# Revit family: Burko F-2750
name_source: partatom
category: HLS-Bauteile
units: mm (PartAtom-declared; Revit-internal decimal feet)

## family parameters
Arbeitsebenenbasiert = Nein
Beim Laden mit Abzugskörper schneiden = Nein
Bemaßung runder Anschluss = Durchmesser verwenden
Beschriftungsausrichtung beibehalten = Nein
Gemeinsam genutzt = Nein
Immer vertikal = Ja
Klassifizierung = Keine
Raumberechnungspunkt = Nein
Teiletyp = Normal

## types (4) — shared parameters
Anschluss_1" = 25 mm  [stored 0.082021 ft]
Anschluss_3/4" = 20 mm  [stored 0.0656168 ft]
Datenblatt = https://www.burkhalter-h2o.ch
Homepage = https://www.burkhalter-h2o.ch
LUT = LUT_Burko_F-2750
Steuerung_Tiefe = 75 mm  [stored 0.246063 ft]
zero-valued in all types: Vorgabe-Ansicht

## per-type parameters (varying)
| type | A | B | Behälterkopf | C | Harzinhalt_pro_Harzdruckbehälter | Hauptsäule_Durchmesser | Sockel_Absatz_Oben | Sockel_Absatz_Unten | Sockel_Höhe | Steuerung_Breite | Steuerung_Höhe |
| Burko F-2750 - 25L | 257 mm  [stored 0.843176 ft] | 1110 mm  [stored 3.64173 ft] | 100 mm  [stored 0.328084 ft] | 1050 mm  [stored 3.44488 ft] | 25L | 75 mm  [stored 0.246063 ft] | 139 mm | 139 mm | 100 mm  [stored 0.328084 ft] | 175 mm  [stored 0.574147 ft] | 150 mm  [stored 0.492126 ft] |
| Burko F-2750 - 50L | 304 mm  [stored 0.997375 ft] | 1440 mm  [stored 4.72441 ft] | 150 mm  [stored 0.492126 ft] | 1380 mm  [stored 4.52756 ft] | 50L | 100 mm  [stored 0.328084 ft] | 162 mm  [stored 0.531496 ft] | 162 mm  [stored 0.531496 ft] | 100 mm  [stored 0.328084 ft] | 175 mm  [stored 0.574147 ft] | 150 mm  [stored 0.492126 ft] |
| Burko F-2750 - 75L | 369 mm  [stored 1.21063 ft] | 1880 mm  [stored 6.16798 ft] | 150 mm  [stored 0.492126 ft] | 1820 mm  [stored 5.97113 ft] | 75L | 100 mm  [stored 0.328084 ft] | 195 mm  [stored 0.639764 ft] | 195 mm  [stored 0.639764 ft] | 100 mm  [stored 0.328084 ft] | 175 mm  [stored 0.574147 ft] | 150 mm  [stored 0.492126 ft] |
| Burko F-2750 - 100L | 406 mm  [stored 1.33202 ft] | 1880 mm  [stored 6.16798 ft] | 150 mm  [stored 0.492126 ft] | 1820 mm  [stored 5.97113 ft] | 100L | 150 mm  [stored 0.492126 ft] | 213 mm  [stored 0.698819 ft] | 213 mm  [stored 0.698819 ft] | 150 mm  [stored 0.492126 ft] | 220 mm  [stored 0.721785 ft] | 175 mm  [stored 0.574147 ft] |

note: [stored X ft] marks values corroborated as IEEE doubles in the binary element streams (Revit-internal decimal feet)
